# Revit family: Mailboxes_4C-Salsbury_Industries-Surface_Mounted-10_Door_High_Units
name_source: partatom
category: Specialty Equipment
units: mm (PartAtom-declared; Revit-internal decimal feet)

## family parameters
Always vertical = Yes
Classification Number = 23.40.90.14.11
Cut with Voids When Loaded = No
Enable Cutting in Views = No
Maintain Annotation Orientation = No
Part Type = Normal
Room Calculation Point = No
Round Connector Dimension = Use Diameter
Shared = No
Work Plane-Based = No

## types (19) — shared parameters
4C Unit Height = 37.5 "
Assembly Code = C1030910
Assembly Description = Mailboxes
Building Codes = https://www.mailboxes.com
Construction Details = https://www.mailboxes.com
Depth = 17.5 "
Green Building-LEED = https://www.arcat.com
Height = 38.594 "
Installation-Fabrication = https://www.mailboxes.com
Keynote = 10 55 00
Lock Material = Stainless Steel - Salsbury Finish -  Polished
Manufacturer = Salsbury Industries
Manufacturer Fax = 1-800-624-5299
Manufacturer Website = https://www.mailboxes.com
MasterFormat Number = 10 55 00
MasterFormat Title = Postal Specialties
OmniClass 23 Number = 23.40.90.14.11
OmniClass 23 Title = Mail Boxes
Product Data = https://www.mailboxes.com
Revision = R1_2018-10
Sales Information = https://www.mailboxes.com
Specification = https://www.mailboxes.com
Test Data = https://www.mailboxes.com
Type Comments = Surface Mounted 4C Horizontal Mailboxes - Front Loading
URL = www.mailboxes.com
Version = 1.0 (06/30/17)
zero-valued in all types: Default Elevation

## per-type parameters (varying)
| type | 4C Unit | 4C Unit Elevation | Above Finished Floor (Bottom of Unit) | Description | Model | Width |
| 3810D-18 | Mailboxes_4C-Salsbury_Industries-Front_Load-10_Door_High_Units : 3710D-18 FL | 26.683 " | 26.12 " | 10 Door High Unit:  18 MB1, OM2 | 3810D-18 | 32.25 " |
| 3810S-08 | Mailboxes_4C-Salsbury_Industries-Front_Load-10_Door_High_Units : 3710S-08 FL | 26.683 " | 26.12 " | 10 Door High Unit:  8 MB1, OM2 | 3810S-08 | 17.496 " |
| 3810D-09 | Mailboxes_4C-Salsbury_Industries-Front_Load-10_Door_High_Units : 3710D-09 FL | 26.683 " | 26.12 " | 10 Door High Unit:  9 MB2, OM2 | 3810D-09 | 32.25 " |
| 3810D-06 | Mailboxes_4C-Salsbury_Industries-Front_Load-10_Door_High_Units : 3710D-06 FL | 26.683 " | 26.12 " | 10 Door High Unit:  6 MB2, 1 PL6, OM2 | 3810D-06 | 32.25 " |
| 3810DA-10 | Mailboxes_4C-Salsbury_Industries-Front_Load-10_Door_High_Units : 3710DA-10 FL | 13.683 " | 13.12 " | 10 Door High Unit:  10 MB1, 1 PL4, 1 PL4.5, OM1.5 | 3810DA-10 | 32.25 " |
| 3810DA-09 | Mailboxes_4C-Salsbury_Industries-Front_Load-10_Door_High_Units : 3710DA-09 FL | 13.683 " | 13.12 " | 10 Door High Unit:  9 MB1, 1 PL4.5, 1 PL5, OM1.5 | 3810DA-09 | 32.25 " |
| 3810D-08 | Mailboxes_4C-Salsbury_Industries-Front_Load-10_Door_High_Units : 3710D-08 FL | 13.683 " | 13.12 " | 10 Door High Unit:  8 MB1, 2 PL5, OM2 | 3810D-08 | 32.25 " |
| 3810D-07 | Mailboxes_4C-Salsbury_Industries-Front_Load-10_Door_High_Units : 3710D-07 FL | 13.683 " | 13.12 " | 10 Door High Unit:  7 MB1, 1 PL5, 1 PL6, OM2 | 3810D-07 | 32.25 " |
| 3810DA-06 | Mailboxes_4C-Salsbury_Industries-Front_Load-10_Door_High_Units : 3710DA-06 FL | 13.683 " | 13.12 " | 10 Door High Unit:  6 MB1, 2 PL6, OM2 | 3810D-06 | 32.25 " |
| 3810D-4P | Mailboxes_4C-Salsbury_Industries-Front_Load-10_Door_High_Units : 3710D-4P FL | 13.683 " | 13.12 " | 10 Door High Unit:  4 PL5 | 3810D-4P | 32.25 " |
| 3810S-04 | Mailboxes_4C-Salsbury_Industries-Front_Load-10_Door_High_Units : 3710S-04 FL | 26.683 " | 26.12 " | 10 Door High Unit:  4 MB2, OM2 | 3810S-04 | 17.496 " |
| 3810SA-04 | Mailboxes_4C-Salsbury_Industries-Front_Load-10_Door_High_Units : 3710SA-04 FL | 13.683 " | 13.12 " | 10 Door High Unit:  4 MB1, 1 PL4.5, OM1.5 | 3810SA-04 | 17.496 " |
| 3810S-03 | Mailboxes_4C-Salsbury_Industries-Front_Load-10_Door_High_Units : 3710S-03 FL | 13.683 " | 13.12 " | 10 Door High Unit:  3 MB1, 1 PL5, OM2 | 3810S-03 | 17.496 " |
| 3810S-02 | Mailboxes_4C-Salsbury_Industries-Front_Load-10_Door_High_Units : 3710S-02 FL | 13.683 " | 13.12 " | 10 Door High Unit:  2 MB1, 1 PL6, OM2 | 3810S-02 | 17.496 " |
| 3810S-01 | Mailboxes_4C-Salsbury_Industries-Front_Load-10_Door_High_Units : 3710S-01 FL | 13.683 " | 13.12 " | 10 Door High Unit:  1 MB3, 1 PL5, OM2 | 3810S-01 | 17.496 " |
| 3810S-2P | Mailboxes_4C-Salsbury_Industries-Front_Load-10_Door_High_Units : 3710S-2P FL | 13.683 " | 13.12 " | 10 Door High Unit:  2 PL5 | 3810S-2P | 17.496 " |
| 3810S-05 | Mailboxes_4C-Salsbury_Industries-Front_Load-10_Door_High_Units : 3710S-05 FL | 13.683 " | 13.12 " | 10 Door High Unit:  5 MB1, 1 PL3, OM2 | 3810S-05 | 17.496 " |
| 3810S-1B | Mailboxes_4C-Salsbury_Industries-Front_Load-10_Door_High_Units : 3710S-1B FL | 13.683 " | 13.12 " | 10 Door High Unit:  1 Receptacle Bin | 3810S-1B | 17.496 " |
| 3810S-1C | Mailboxes_4C-Salsbury_Industries-Front_Load-10_Door_High_Units : 3710S-1C FL | 13.683 " | 13.12 " | 10 Door High Unit:  1 Collection Box | 3810S-1C | 17.496 " |

## geometry (parser evidence)
native form markers: Blend x2, Extrusion x4, Sweep x20
no freeform markers — native parametric forms only
